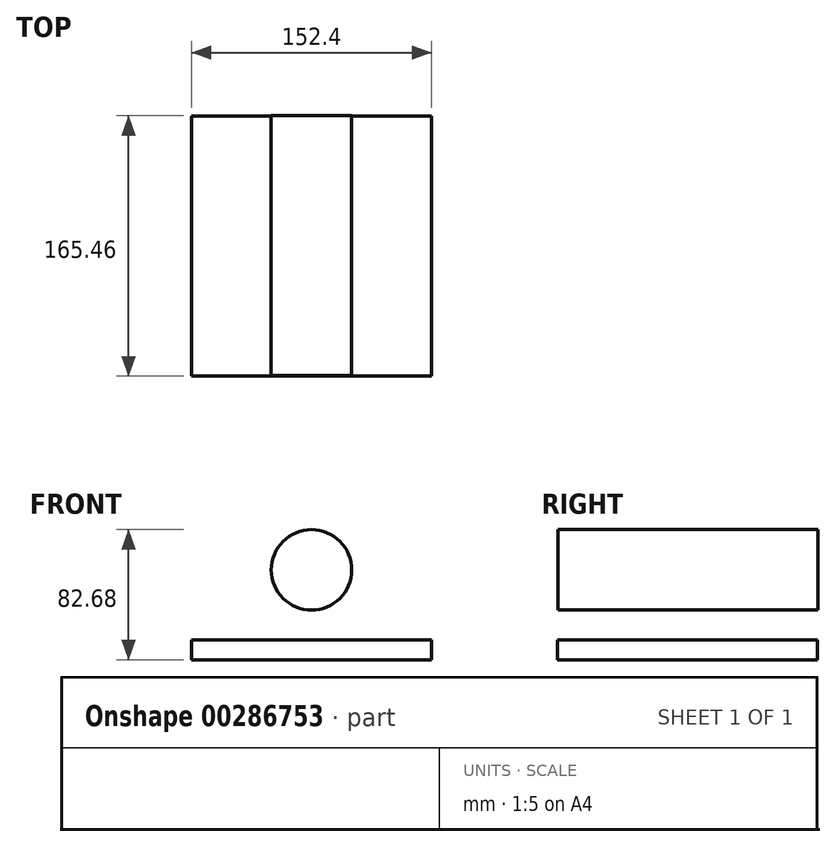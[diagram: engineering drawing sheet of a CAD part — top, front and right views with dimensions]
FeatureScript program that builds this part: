
annotation { "Feature Type Name" : "Feature", "Feature Type Description" : "" }
export const myFeature = defineFeature(function(context is Context, id is Id, definition is map)
    precondition{}
    {
        {
            var Q0;
            Q0=qCreatedBy(makeId("Right.planeOp"),FACE);
            var sketch = newSketch(context, id + "F0", { "sketchPlane" : qUnion([Q0])});
            skLineSegment(sketch, "E0.bottom", {"start": v(-81.64, 0) * mm, "end": v(83.46, 0) * mm});
            skLineSegment(sketch, "E0.top", {"start": v(-81.64, -12.7) * mm, "end": v(83.46, -12.7) * mm});
            skLineSegment(sketch, "E0.left", {"start": v(-81.64, 0) * mm, "end": v(-81.64, -12.7) * mm});
            skLineSegment(sketch, "E0.right", {"start": v(83.46, 0) * mm, "end": v(83.46, -12.7) * mm});
            skLineSegment(sketch, "E1.bottom", {"start": v(-81.64, 0) * mm, "end": v(-68.94, 0) * mm});
            skLineSegment(sketch, "E1.top", {"start": v(-81.64, 101.6) * mm, "end": v(-68.94, 101.6) * mm});
            skLineSegment(sketch, "E1.left", {"start": v(-81.64, 0) * mm, "end": v(-81.64, 101.6) * mm});
            skLineSegment(sketch, "E1.right", {"start": v(-68.94, 0) * mm, "end": v(-68.94, 101.6) * mm});
            skLineSegment(sketch, "E2.bottom", {"start": v(-30.84, 0) * mm, "end": v(-18.14, 0) * mm});
            skLineSegment(sketch, "E2.top", {"start": v(-30.84, 88.9) * mm, "end": v(-18.14, 88.9) * mm});
            skLineSegment(sketch, "E2.left", {"start": v(-30.84, 0) * mm, "end": v(-30.84, 88.9) * mm});
            skLineSegment(sketch, "E2.right", {"start": v(-18.14, 0) * mm, "end": v(-18.14, 88.9) * mm});
            skLineSegment(sketch, "E3.bottom", {"start": v(19.96, 0) * mm, "end": v(32.66, 0) * mm});
            skLineSegment(sketch, "E3.top", {"start": v(19.96, 50.8) * mm, "end": v(32.66, 50.8) * mm});
            skLineSegment(sketch, "E3.left", {"start": v(19.96, 0) * mm, "end": v(19.96, 50.8) * mm});
            skLineSegment(sketch, "E3.right", {"start": v(32.66, 0) * mm, "end": v(32.66, 50.8) * mm});
            skLineSegment(sketch, "E4.bottom", {"start": v(70.76, 0) * mm, "end": v(83.46, 0) * mm});
            skLineSegment(sketch, "E4.top", {"start": v(70.76, 25.4) * mm, "end": v(83.46, 25.4) * mm});
            skLineSegment(sketch, "E4.left", {"start": v(70.76, 0) * mm, "end": v(70.76, 25.4) * mm});
            skLineSegment(sketch, "E4.right", {"start": v(83.46, 0) * mm, "end": v(83.46, 25.4) * mm});
            skSolve(sketch);
        }
        {
            var Q0;
            Q0=makeQuery(id+"F0.imprint","IMPRINT",FACE,{"disambiguationData":[TD([[makeQuery(id+"F0.imprint","IMPRINT",EDGE,{"derivedFrom":sQuery(id+"F0.wireOp",EDGE,"E0.top")}),1.0]])]});
            var Q1;
            Q1=makeQuery(id+"F0.imprint","IMPRINT",FACE,{"disambiguationData":[TD([[makeQuery(id+"F0.imprint","IMPRINT",EDGE,{"derivedFrom":sQuery(id+"F0.wireOp",EDGE,"E4.bottom")}),1.0]])]});
            var Q2;
            Q2=makeQuery(id+"F0.imprint","IMPRINT",FACE,{"disambiguationData":[TD([[makeQuery(id+"F0.imprint","IMPRINT",EDGE,{"derivedFrom":sQuery(id+"F0.wireOp",EDGE,"E3.bottom")}),1.0]])]});
            var Q3;
            Q3=makeQuery(id+"F0.imprint","IMPRINT",FACE,{"disambiguationData":[TD([[makeQuery(id+"F0.imprint","IMPRINT",EDGE,{"derivedFrom":sQuery(id+"F0.wireOp",EDGE,"E2.bottom")}),1.0]])]});
            var Q4;
            Q4=makeQuery(id+"F0.imprint","IMPRINT",FACE,{"disambiguationData":[TD([[makeQuery(id+"F0.imprint","IMPRINT",EDGE,{"derivedFrom":sQuery(id+"F0.wireOp",EDGE,"E1.bottom")}),1.0]])]});
            extrude(context, id + "F1", {"entities" : qUnion([Q0, Q1, Q2, Q3, Q4]), "offsetDistance" : 25.4 * mm, "depth" : 152.4 * mm});
        }
        {
            var Q0;
            Q0=qCreatedBy(makeId("Front.planeOp"),FACE);
            var sketch = newSketch(context, id + "F2", { "sketchPlane" : qUnion([Q0])});
            skCircle(sketch, "E5", {"center": v(76.2, 44.45) * mm, "radius": 25.53 * mm});
            skSolve(sketch);
        }
        {
            var Q0;
            Q0=makeQuery(id+"F2.imprint","IMPRINT",FACE,{"disambiguationData":[TD([[makeQuery(id+"F2.imprint","IMPRINT",EDGE,{"derivedFrom":sQuery(id+"F2.wireOp",EDGE,"E5")}),1.0]])]});
            extrude(context, id + "F3", {"entities" : qUnion([Q0]), "operationType" : NewBodyOperationType.ADD, "offsetDistance" : 25.4 * mm, "depth" : 81.28 * mm, "hasSecondDirection" : true, "secondDirectionOppositeDirection" : true, "secondDirectionDepth" : 83.82 * mm});
        }
    });
